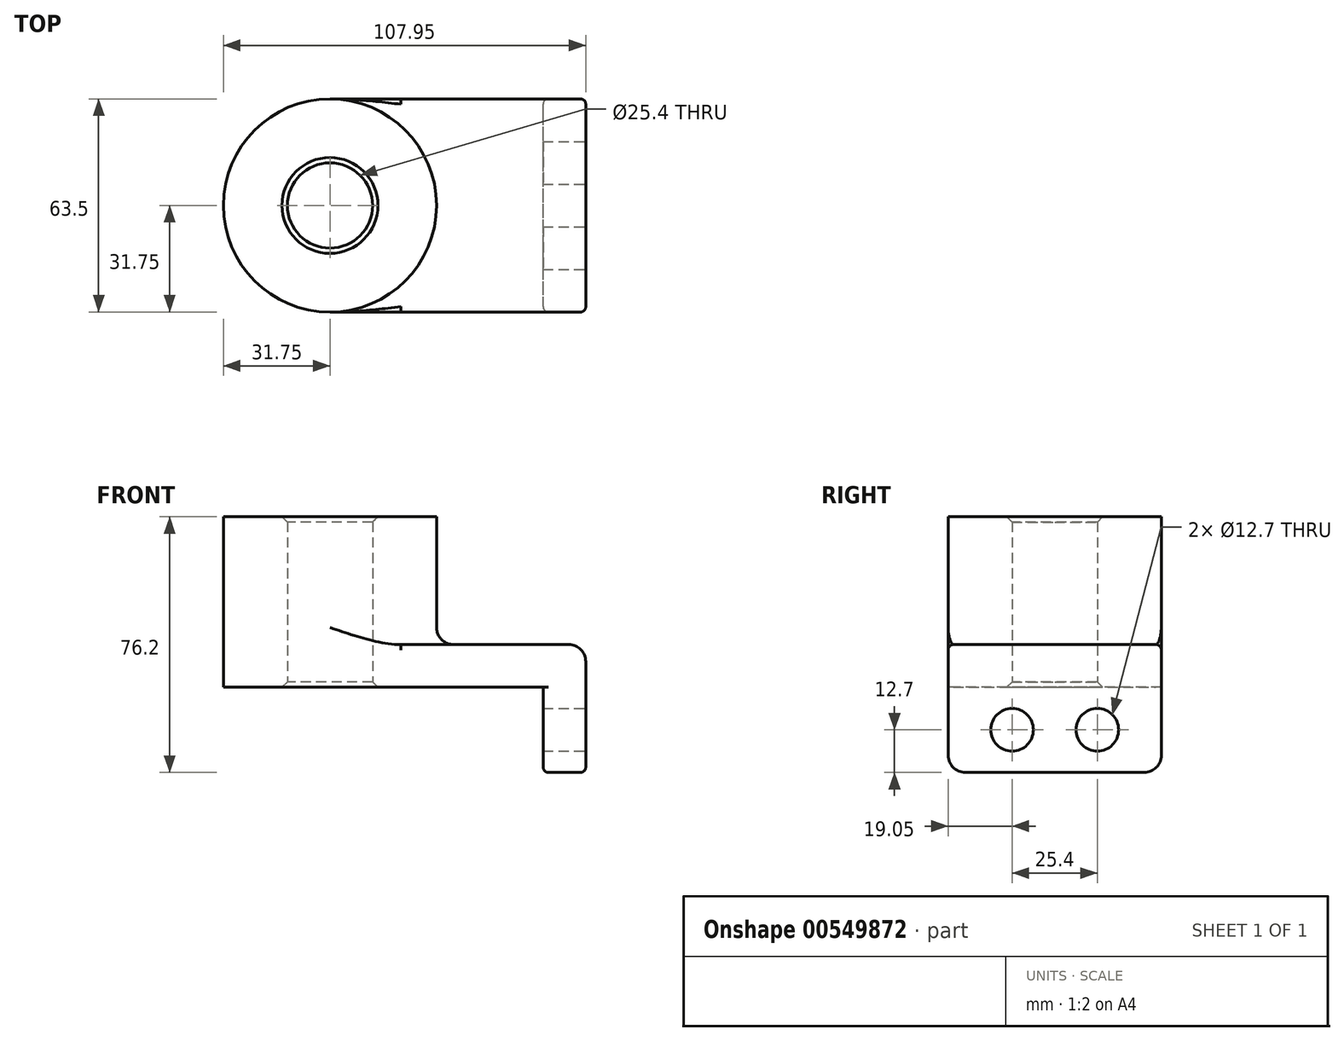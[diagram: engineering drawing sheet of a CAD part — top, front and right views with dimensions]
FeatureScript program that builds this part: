
annotation { "Feature Type Name" : "Feature", "Feature Type Description" : "" }
export const myFeature = defineFeature(function(context is Context, id is Id, definition is map)
    precondition{}
    {
        {
            var Q0;
            Q0=qCreatedBy(makeId("Top.planeOp"),FACE);
            var sketch = newSketch(context, id + "F0", { "sketchPlane" : qUnion([Q0])});
            skLineSegment(sketch, "E0.bottom", {"start": v(38.1, -31.75) * mm, "end": v(-38.1, -31.75) * mm});
            skLineSegment(sketch, "E0.top", {"start": v(38.1, 31.75) * mm, "end": v(-38.1, 31.75) * mm});
            skLineSegment(sketch, "E0.left", {"start": v(38.1, -31.75) * mm, "end": v(38.1, 31.75) * mm});
            skLineSegment(sketch, "E0.right", {"start": v(-38.1, -31.75) * mm, "end": v(-38.1, 31.75) * mm});
            skPoint(sketch, "E0.middle", {"position": v(0, 0) * mm});
            skCircle(sketch, "E1", {"center": v(-38.1, 0) * mm, "radius": 31.75 * mm});
            skCircle(sketch, "E2", {"center": v(-38.1, 0) * mm, "radius": 12.7 * mm});
            skSolve(sketch);
        }
        {
            var Q0;
            Q0 = qSketchRegion(id + "F0", true);
            extrude(context, id + "F1", {"entities" : qUnion([Q0]), "depth" : 12.7 * mm, "offsetDistance" : 25.4 * mm});
        }
        {
            var Q0;
            {var subQ1=sQuery(id+"F0.wireOp",EDGE,"E0.right");var subQ3=sQuery(id+"F0.wireOp",EDGE,"E2");var subQ4=makeQuery(id+"F0.imprint","INTERSECT",VERTEX,{"disambiguationData":[OD(0.0)],"derivedFrom":[subQ1,subQ3]});Q0=makeQuery(id+"F0.imprint","IMPRINT",FACE,{"disambiguationData":[TD([[makeQuery(id+"F0.imprint","IMPRINT",EDGE,{"disambiguationData":[TD([[subQ4,1.0]])],"derivedFrom":subQ3}),-1.0]])]});}
            var Q1;
            {var subQ1=sQuery(id+"F0.wireOp",EDGE,"E0.right");var subQ3=sQuery(id+"F0.wireOp",EDGE,"E2");var subQ4=makeQuery(id+"F0.imprint","INTERSECT",VERTEX,{"disambiguationData":[OD(0.0)],"derivedFrom":[subQ1,subQ3]});Q1=makeQuery(id+"F0.imprint","IMPRINT",FACE,{"disambiguationData":[TD([[makeQuery(id+"F0.imprint","IMPRINT",EDGE,{"disambiguationData":[TD([[subQ4,-1.0]])],"derivedFrom":subQ3}),-1.0]])]});}
            extrude(context, id + "F2", {"entities" : qUnion([Q0, Q1]), "operationType" : NewBodyOperationType.ADD, "depth" : 50.8 * mm, "offsetDistance" : 25.4 * mm});
        }
        {
            var Q0;
            Q0=makeQuery(id+"F1.opExtrude","SWEPT_FACE",FACE,{"disambiguationData":[OSD([sQuery(id+"F0.wireOp",EDGE,"E0.left")])]});
            var sketch = newSketch(context, id + "F3", { "sketchPlane" : qUnion([Q0])});
            skLineSegment(sketch, "E3.bottom", {"start": v(-31.75, 12.7) * mm, "end": v(31.75, 12.7) * mm});
            skLineSegment(sketch, "E3.top", {"start": v(-31.75, -25.4) * mm, "end": v(31.75, -25.4) * mm});
            skLineSegment(sketch, "E3.left", {"start": v(-31.75, 12.7) * mm, "end": v(-31.75, -25.4) * mm});
            skLineSegment(sketch, "E3.right", {"start": v(31.75, 12.7) * mm, "end": v(31.75, -25.4) * mm});
            skCircle(sketch, "E4", {"center": v(-12.7, -12.7) * mm, "radius": 6.35 * mm});
            skLineSegment(sketch, "E5", {"start": v(0, -0.99) * mm, "end": v(0, -25.4) * mm, "construction": true});
            skPoint(sketch, "E5.startSnap0", {"position": v(0, 0) * mm});
            skCircle(sketch, "E6.MirrorC", {"center": v(12.7, -12.7) * mm, "radius": 6.35 * mm});
            skSolve(sketch);
        }
        {
            var Q0;
            {var subQ2=sQuery(id+"F3.wireOp",EDGE,"E3.top");Q0=makeQuery(id+"F3.imprint","IMPRINT",FACE,{"disambiguationData":[TD([[makeQuery(id+"F3.imprint","IMPRINT",EDGE,{"derivedFrom":subQ2}),1.0]])]});}
            extrude(context, id + "F4", {"entities" : qUnion([Q0]), "operationType" : NewBodyOperationType.ADD, "oppositeDirection" : true, "depth" : 12.7 * mm, "offsetDistance" : 25.4 * mm});
        }
        {
            var Q0;
            {var subQ0=sQuery(id+"F0.wireOp",EDGE,"E1");Q0=makeQuery(id+"F2.boolean.opBoolean","INTERSECT",EDGE,{"derivedFrom":[makeQuery(id+"F1.opExtrude","CAP_FACE",FACE,{"disambiguationData":[OSD([sQuery(id+"F0.wireOp",EDGE,"E0.bottom"),sQuery(id+"F0.wireOp",EDGE,"E0.top"),sQuery(id+"F0.wireOp",EDGE,"E0.left"),subQ0,sQuery(id+"F0.wireOp",EDGE,"E2")])],"isStart":false}),makeQuery(id+"F2.opExtrude","SWEPT_FACE",FACE,{"disambiguationData":[OSD([subQ0])]})]});}
            var Q1;
            Q1=makeQuery(id+"F1.opExtrude","CAP_EDGE",EDGE,{"disambiguationData":[OSD([sQuery(id+"F0.wireOp",EDGE,"E0.left")])],"isStart":false});
            var Q2;
            Q2=makeQuery(id+"F4.opExtrude","SWEPT_EDGE",EDGE,{"disambiguationData":[OSD([sQuery(id+"F3.wireOp",EDGE,"E3.top"),sQuery(id+"F3.wireOp",EDGE,"E3.left")])]});
            var Q3;
            Q3=makeQuery(id+"F4.opExtrude","SWEPT_EDGE",EDGE,{"disambiguationData":[OSD([sQuery(id+"F3.wireOp",EDGE,"E3.top"),sQuery(id+"F3.wireOp",EDGE,"E3.right")])]});
            fillet(context, id + "F5", {"entities" : qUnion([Q0, Q1, Q2, Q3]), "radius" : 5.08 * mm, "tangentPropagation" : true, "allowEdgeOverflow" : false});
        }
        {
            var Q0;
            Q0=makeQuery(id+"F1.opExtrude","CAP_EDGE",EDGE,{"disambiguationData":[OSD([sQuery(id+"F0.wireOp",EDGE,"E0.bottom")])],"isStart":false});
            var Q1;
            Q1=makeQuery(id+"F4.opExtrude","CAP_EDGE",EDGE,{"disambiguationData":[OSD([sQuery(id+"F3.wireOp",EDGE,"E3.left")])],"isStart":false});
            var Q2;
            Q2=makeQuery(id+"F4.opExtrude","CAP_EDGE",EDGE,{"disambiguationData":[OSD([sQuery(id+"F0.wireOp",EDGE,"E0.left")])],"isStart":false});
            fillet(context, id + "F6", {"entities" : qUnion([Q0, Q1, Q2]), "radius" : 1.59 * mm, "tangentPropagation" : true, "allowEdgeOverflow" : false});
        }
        {
            var Q0;
            {var subQ0=sQuery(id+"F0.wireOp",EDGE,"E2");Q0=makeQuery(id+"F2.boolean.opBoolean","MERGE",FACE,{"derivedFrom":[makeQuery(id+"F1.opExtrude","SWEPT_FACE",FACE,{"disambiguationData":[OSD([subQ0])]}),makeQuery(id+"F2.opExtrude","SWEPT_FACE",FACE,{"disambiguationData":[OSD([subQ0])]})]});}
            chamfer(context, id + "F7", {"entities" : qUnion([Q0]), "width" : 1.59 * mm, "tangentPropagation" : true});
        }
    });
